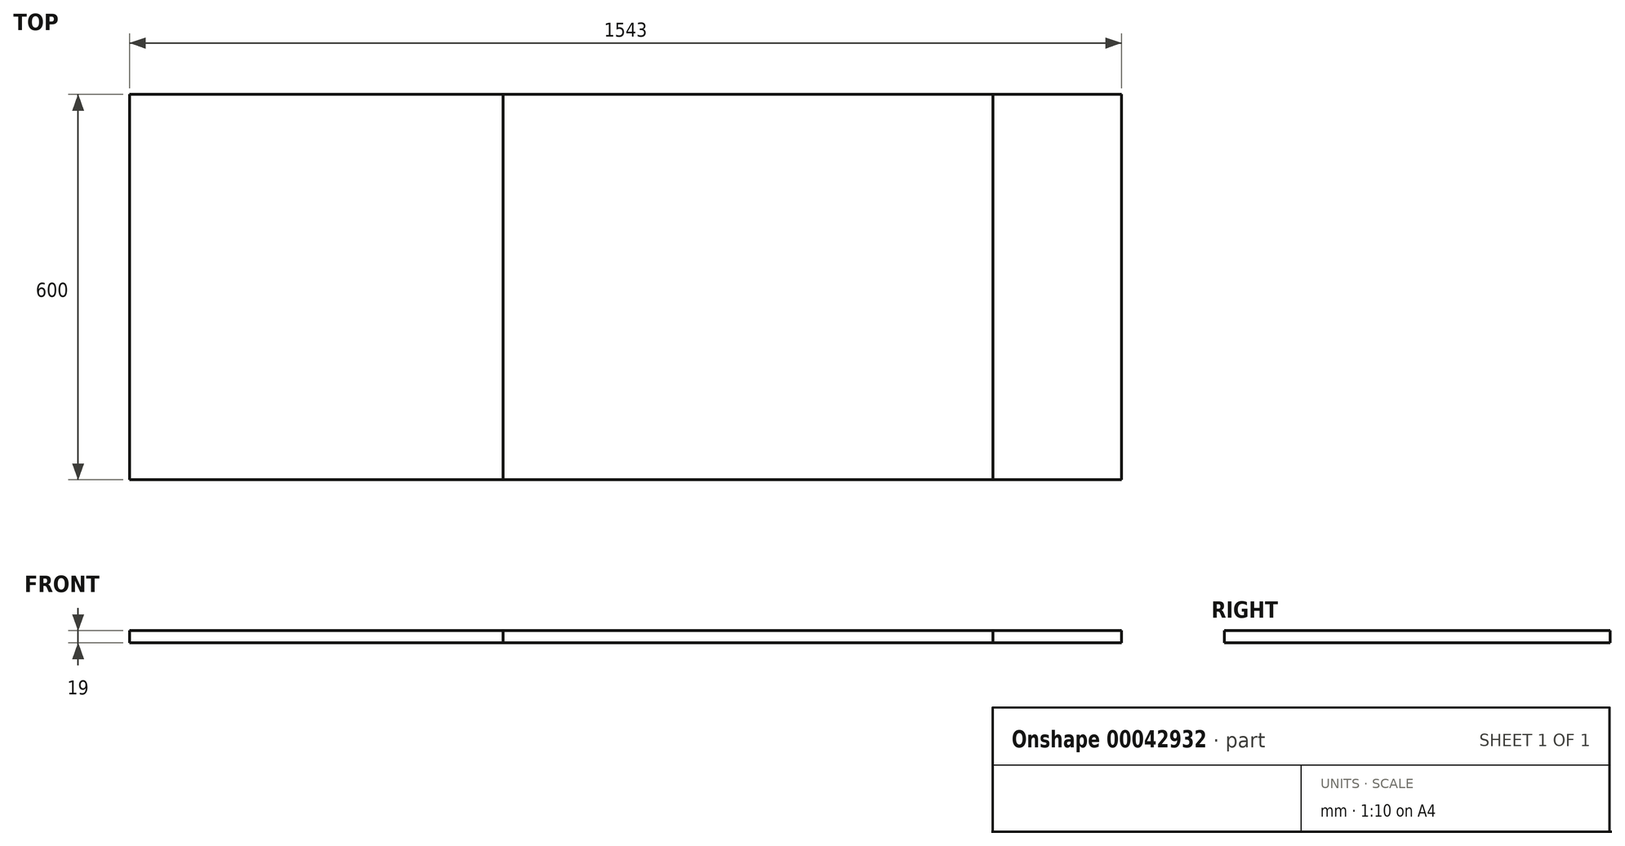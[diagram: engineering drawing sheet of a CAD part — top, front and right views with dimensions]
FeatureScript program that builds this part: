
annotation { "Feature Type Name" : "Feature", "Feature Type Description" : "" }
export const myFeature = defineFeature(function(context is Context, id is Id, definition is map)
    precondition{}
    {
        {
            assignVariable(context, id + "F0", {"name" : "CupboardThickness", "anyValue" : 19});
        }
        {
            var Q0;
            Q0=qCreatedBy(makeId("Right.planeOp"),FACE);
            var sketch = newSketch(context, id + "F1", { "sketchPlane" : qUnion([Q0])});
            skLineSegment(sketch, "E0.bottom", {"start": v(0, 0) * mm, "end": v(600, 0) * mm});
            skLineSegment(sketch, "E0.top", {"start": v(0, 19) * mm, "end": v(600, 19) * mm});
            skLineSegment(sketch, "E0.left", {"start": v(0, 0) * mm, "end": v(0, 19) * mm});
            skLineSegment(sketch, "E0.right", {"start": v(600, 0) * mm, "end": v(600, 19) * mm});
            skSolve(sketch);
        }
        {
            var Q0;
            Q0=makeQuery(id+"F1.imprint","IMPRINT",FACE,{"disambiguationData":[TD([[makeQuery(id+"F1.imprint","IMPRINT",EDGE,{"derivedFrom":sQuery(id+"F1.wireOp",EDGE,"E0.bottom")}),1.0]])]});
            extrude(context, id + "F2", {"entities" : qUnion([Q0]), "depth" : (800 - 2 * getVariable(context, 'CupboardThickness')) * mm});
        }
        {
            var Q0;
            Q0=makeQuery(id+"F2.opExtrude","CAP_FACE",FACE,{"disambiguationData":[OSD([sQuery(id+"F1.wireOp",EDGE,"E0.bottom"),sQuery(id+"F1.wireOp",EDGE,"E0.top"),sQuery(id+"F1.wireOp",EDGE,"E0.left"),sQuery(id+"F1.wireOp",EDGE,"E0.right")])],"isStart":true});
            extrude(context, id + "F3", {"entities" : qUnion([Q0]), "depth" : ((2000 - 800 - 2 * getVariable(context, 'CupboardThickness')) / 2) * mm});
        }
        {
            var Q0;
            Q0 = qSketchRegion(id + "F1", true);
            extrude(context, id + "F4", {"entities" : qUnion([Q0]), "depth" : (1000 - 2 * getVariable(context, 'CupboardThickness')) * mm});
        }
    });
